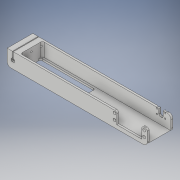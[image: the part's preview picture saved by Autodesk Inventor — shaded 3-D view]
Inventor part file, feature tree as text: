
AUTODESK INVENTOR PART (.ipt)
format: ipt  version: 2017 (Build 210142000, 142)  size: 359,424 bytes
history: native  units: in
note: dims shown in document units (in); Inventor stores cm internally (conversion verified against a paired STEP export)
features: sketch x9, projected_geometry x7, extrude x6, fillet x5, hole x3
ambient origin geometry x8: Origin, YZ Plane, XZ Plane, XY Plane, X Axis, Y Axis, Z Axis, Center Point
bodies: Solid1 (feature_tree)
feature tree (30):
  extrude  "Extrusion1"  Depth=1.685in
  extrude  "Extrusion2"  Depth=1.435in
  extrude  "Extrusion4"  Depth=9.197in TaperAngle=0.0deg
  extrude  "Extrusion5"  Depth=1.0in
  hole  "Hole1"  [1 undecoded]
  hole  "Hole2"  [1 undecoded]
  fillet  "Fillet1"  Radius=0.164in
  fillet  "Fillet2"  Radius=0.3937in
  fillet  "Fillet3"  Radius=0.19in
  extrude  "Extrusion6"  Depth=0.5in TaperAngle=0.0deg
  fillet  "Fillet4"  Radius=0.75in
  extrude  "Extrusion7"  Depth=0.078in
  fillet  "Fillet5"  Radius=0.078in
  hole  "Hole5"  [1 undecoded]
  sketch  "Sketch1"  dims[d0=1.0in d1=1.685in]
  sketch  "Sketch2"  dims[d2=0.875in d3=1.435in]
  projected_geometry  "Projected Loop1"
  sketch  "Sketch4"  dims[d4=0.125in d5=9.197in d6=0.0in]
  projected_geometry  "Projected Loop3"
  sketch  "Sketch5"  dims[d7=0.35in d8=1.0in]
  sketch  "Sketch6"  dims[d9=0.75in d10=2.0in]
  projected_geometry  "Projected Loop4"
  sketch  "Sketch7"  dims[d11=0.19in d12=0.19in d13=0.164in d14=0.3937in d15=0.19in]
  projected_geometry  "Projected Loop5"
  sketch  "Sketch9"  dims[d16=0.19in d19=0.5in d20=0.0in d26=0.75in]
  projected_geometry  "Projected Loop7"
  sketch  "Sketch10"  dims[d27=0.133in d28=0.078in d29=0.078in]
  projected_geometry  "Projected Loop8"
  sketch  "Sketch11"  dims[d30=0.098in d31=0.236in d32=0.0665in d33=0.0665in d34=0.0665in d35=0.0in d36=0.118in d37=0.133in d38=1.0in d39=0.5in d40=0.375in d41=0.05in d42=0.35in d43=1.685in d44=0.0in d45=0.75in d46=0.078in d47=0.078in d48=0.098in d49=0.0665in d50=0.0665in d51=0.0665in d52=0.0in d53=0.133in d54=1.0in d55=0.5in d56=0.375in d57=0.35in d58=0.133in d59=0.05in d60=1.685in d61=0.0in d62=0.25in d63=0.25in d64=1.685in d65=0.25in d66=0.8425in d67=0.2106in d68=0.2106in d69=0.158in d70=0.75in d71=0.375in d72=0.25in d73=0.5635in d74=0.355in d75=0.8108in d76=0.104in d77=0.276in d78=0.375in d79=0.25in d80=0.5635in d81=0.432in d82=0.8108in d83=0.125in d91=1.9488in d92=1.9488in d93=0.164in d95=0.3937in d96=0.197in d97=0.197in d105=0.25in d106=0.125in d107=1.685in d108=8.697in d109=0.5in d110=0.25in d111=1.185in d112=3.5985in d113=1.0in d114=0.0in d119=0.125in d121=0.774in d122=0.546in d125=0.2756in d126=1.0in d127=0.4229in d128=0.0969in d129=0.0969in d130=0.0in d131=0.621in d132=0.376in d133=0.25in d134=0.0in d135=0.1352in d136=0.0969in d137=0.0969in d138=0.376in d139=0.936in d140=0.936in d141=0.1in d142=0.097in d143=0.75in d144=0.2362in d145=0.25in d146=90.0deg d147=1.0in d148=0.8108in]
  projected_geometry  "Projected Loop9"
note: 3 required parameter values undecoded (feature->parameter linkage not recoverable at this tier; creation-order binding heuristic only, values carry confidence <= 0.55)
